# Revit family: Breezy_Eng
name_source: partatom
category: Mechanical Equipment
units: mm (PartAtom-declared; Revit-internal decimal feet)

## family parameters
Always vertical = Yes
Classification = None
Cut with Voids When Loaded = No
Part Type = Normal
Room Calculation Point = No
Round Connector Dimension = Use Diameter
Shared = No
Work Plane-Based = No

## types (2) — shared parameters
00_20_Manufacturer = Vents
00_20_Name = Smart HRV units for single-room ventilation
Casing Material = Plastic, opaque, white
Frequency = 50 Hz
Height = 305 mm  [stored 1.00066 ft]
Length = 612 mm  [stored 2.00787 ft]
Load Classification = HVAC
Maintenance zone material = <By Category>
Manufacturer = Vents
Number of Fase = 1
Power = 100 W
URL = https://ventilation-system.com
Voltage = 230 V
Width = 245 mm  [stored 0.803806 ft]
l = 450 mm  [stored 1.47638 ft]
zero-valued in all types: Default Elevation

## per-type parameters (varying)
| type | -R1 | -r | D1 | Dn | Dy | Maximum Air Flow | R1 | Sound pressure level at 3 m distance | Weight |
| Breezy 160 | -95 mm | -55 mm  [stored -0.180446 ft] | 190 mm | 165 mm | 160 mm  [stored 0.524934 ft] | 57.0 m³/h | 95 mm  [stored 0.31168 ft] | 35 dBA | 6.50 kg |
| Breezy 200 | -115 mm  [stored -0.377297 ft] | -75 mm | 230 mm  [stored 0.754593 ft] | 205 mm  [stored 0.672572 ft] | 200 mm  [stored 0.656168 ft] | 95.0 m³/h | 115 mm  [stored 0.377297 ft] | 34 dBA | 7.00 kg |

note: column(s) folded — value = type name in every type: 00_20_Type

note: [stored X ft] marks values corroborated as IEEE doubles in the binary element streams (Revit-internal decimal feet)
